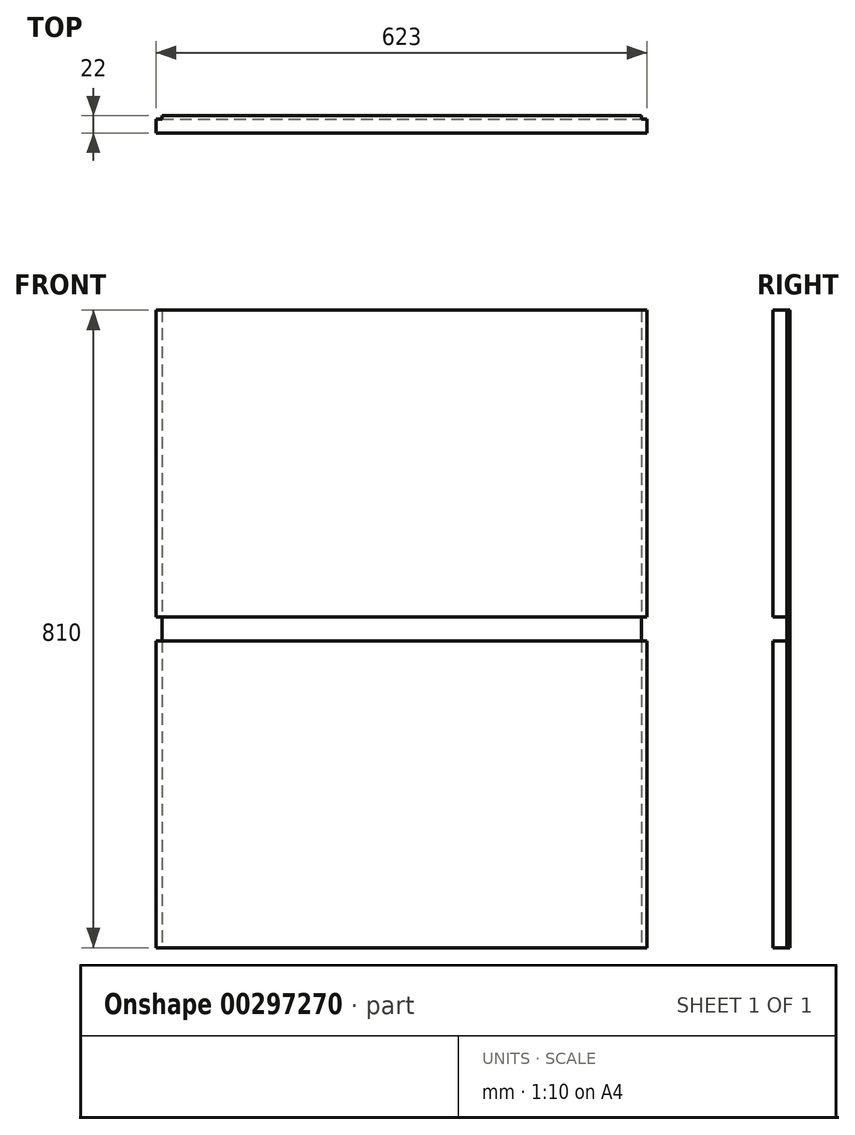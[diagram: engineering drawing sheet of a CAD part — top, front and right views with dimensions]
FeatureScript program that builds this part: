
annotation { "Feature Type Name" : "Feature", "Feature Type Description" : "" }
export const myFeature = defineFeature(function(context is Context, id is Id, definition is map)
    precondition{}
    {
        {
            var Q0;
            Q0=qCreatedBy(makeId("Front.planeOp"),FACE);
            var sketch = newSketch(context, id + "F0", { "sketchPlane" : qUnion([Q0])});
            skLineSegment(sketch, "E0.bottom", {"start": v(-311.5, 405) * mm, "end": v(311.5, 405) * mm});
            skLineSegment(sketch, "E0.top", {"start": v(-311.5, -405) * mm, "end": v(311.5, -405) * mm});
            skLineSegment(sketch, "E0.left", {"start": v(-311.5, 405) * mm, "end": v(-311.5, -405) * mm});
            skLineSegment(sketch, "E0.right", {"start": v(311.5, 405) * mm, "end": v(311.5, -405) * mm});
            skPoint(sketch, "E0.middle", {"position": v(0, 0) * mm});
            skSolve(sketch);
        }
        {
            var Q0;
            Q0 = qSketchRegion(id + "F0", true);
            extrude(context, id + "F1", {"entities" : qUnion([Q0]), "depth" : 22 * mm});
        }
        {
            var Q0;
            Q0=makeQuery(id+"F1.opExtrude","SWEPT_FACE",FACE,{"disambiguationData":[OSD([sQuery(id+"F0.wireOp",EDGE,"E0.right")])]});
            var sketch = newSketch(context, id + "F2", { "sketchPlane" : qUnion([Q0])});
            skLineSegment(sketch, "E1.bottom", {"start": v(-22, -15) * mm, "end": v(-4, -15) * mm});
            skLineSegment(sketch, "E1.top", {"start": v(-22, 15) * mm, "end": v(-4, 15) * mm});
            skLineSegment(sketch, "E1.left", {"start": v(-22, -15) * mm, "end": v(-22, 15) * mm});
            skLineSegment(sketch, "E1.right", {"start": v(-4, -15) * mm, "end": v(-4, 15) * mm});
            skSolve(sketch);
        }
        {
            var Q0;
            Q0 = qSketchRegion(id + "F2", true);
            extrude(context, id + "F3", {"entities" : qUnion([Q0]), "operationType" : NewBodyOperationType.REMOVE, "oppositeDirection" : true, "depth" : 623 * mm});
        }
        {
            var Q0;
            Q0=makeQuery(id+"F1.opExtrude","CAP_FACE",FACE,{"disambiguationData":[OSD([sQuery(id+"F0.wireOp",EDGE,"E0.bottom"),sQuery(id+"F0.wireOp",EDGE,"E0.top"),sQuery(id+"F0.wireOp",EDGE,"E0.left"),sQuery(id+"F0.wireOp",EDGE,"E0.right")])],"isStart":true});
            var sketch = newSketch(context, id + "F4", { "sketchPlane" : qUnion([Q0])});
            skLineSegment(sketch, "E2.bottom", {"start": v(-311.5, 405) * mm, "end": v(-304.5, 405) * mm});
            skLineSegment(sketch, "E2.top", {"start": v(-311.5, -405) * mm, "end": v(-304.5, -405) * mm});
            skLineSegment(sketch, "E2.left", {"start": v(-311.5, 405) * mm, "end": v(-311.5, -405) * mm});
            skLineSegment(sketch, "E2.right", {"start": v(-304.5, 405) * mm, "end": v(-304.5, -405) * mm});
            skLineSegment(sketch, "E3.bottom", {"start": v(311.5, 405) * mm, "end": v(304.5, 405) * mm});
            skLineSegment(sketch, "E3.top", {"start": v(311.5, -405) * mm, "end": v(304.5, -405) * mm});
            skLineSegment(sketch, "E3.left", {"start": v(311.5, 405) * mm, "end": v(311.5, -405) * mm});
            skLineSegment(sketch, "E3.right", {"start": v(304.5, 405) * mm, "end": v(304.5, -405) * mm});
            skSolve(sketch);
        }
        {
            var Q0;
            Q0 = qSketchRegion(id + "F4", true);
            extrude(context, id + "F5", {"entities" : qUnion([Q0]), "operationType" : NewBodyOperationType.REMOVE, "oppositeDirection" : true, "depth" : 4 * mm});
        }
    });
